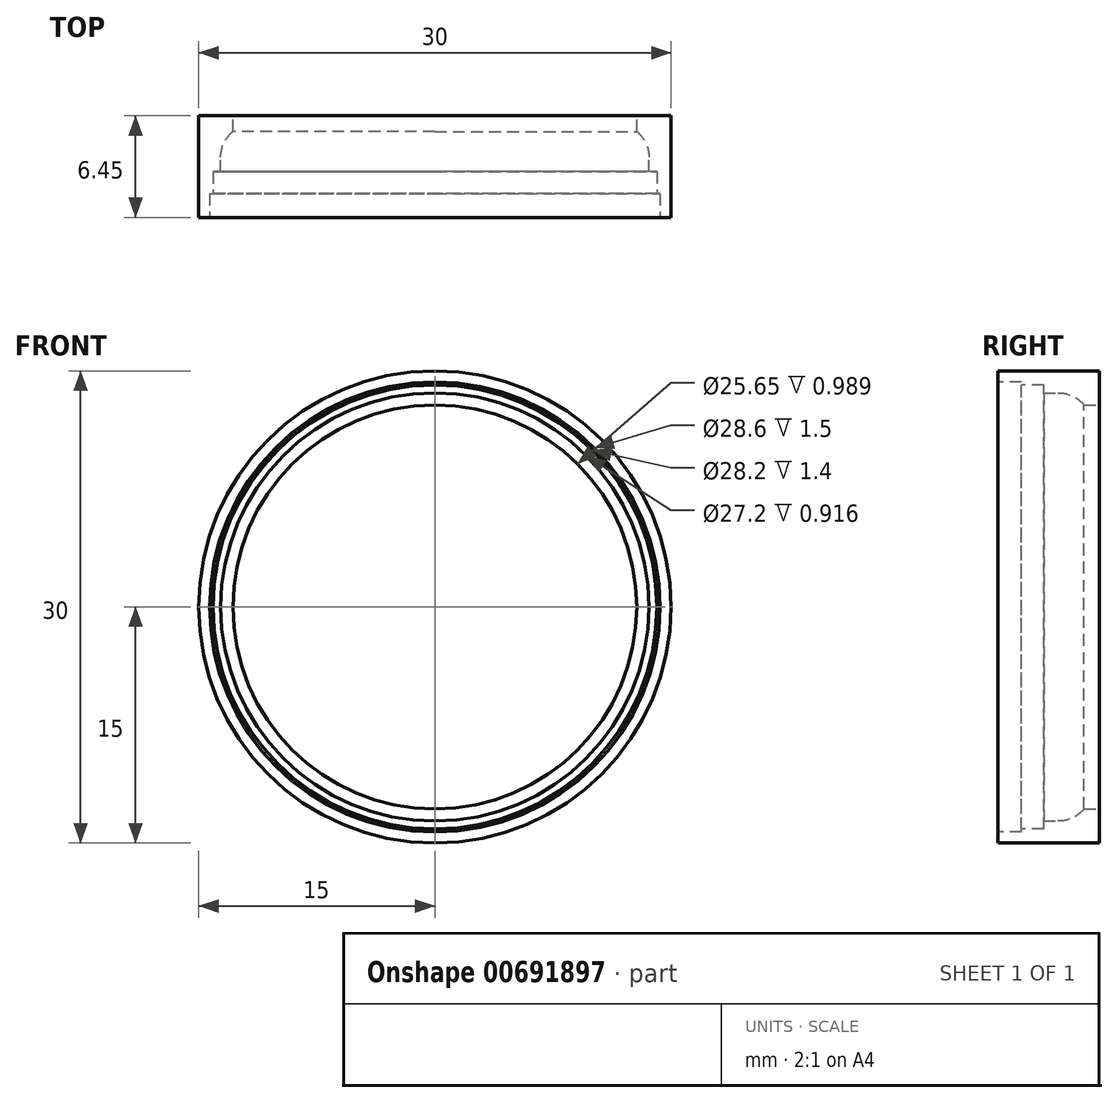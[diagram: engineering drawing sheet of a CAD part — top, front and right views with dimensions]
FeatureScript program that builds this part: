
annotation { "Feature Type Name" : "Feature", "Feature Type Description" : "" }
export const myFeature = defineFeature(function(context is Context, id is Id, definition is map)
    precondition{}
    {
        {
            var Q0;
            Q0=qCreatedBy(makeId("Front.planeOp"),FACE);
            var sketch = newSketch(context, id + "F0", { "sketchPlane" : qUnion([Q0])});
            skCircle(sketch, "E0", {"center": v(0, 0) * mm, "radius": 15 * mm});
            skCircle(sketch, "E1", {"center": v(0, 0) * mm, "radius": 12.82 * mm});
            skSolve(sketch);
        }
        {
            var Q0;
            Q0 = qSketchRegion(id + "F0", true);
            extrude(context, id + "F1", {"entities" : qUnion([Q0]), "depth" : 6.45 * mm, "offsetDistance" : 25.4 * mm});
        }
        {
            var Q0;
            Q0=makeQuery(id+"F1.opExtrude","CAP_FACE",FACE,{"disambiguationData":[OSD([sQuery(id+"F0.wireOp",EDGE,"E0"),sQuery(id+"F0.wireOp",EDGE,"E1")])],"isStart":false});
            var sketch = newSketch(context, id + "F2", { "sketchPlane" : qUnion([Q0])});
            skCircle(sketch, "E2", {"center": v(0, 0) * mm, "radius": 14.3 * mm});
            skSolve(sketch);
        }
        {
            var Q0;
            Q0 = qSketchRegion(id + "F2", true);
            extrude(context, id + "F3", {"entities" : qUnion([Q0]), "operationType" : NewBodyOperationType.REMOVE, "oppositeDirection" : true, "depth" : 1.5 * mm, "offsetDistance" : 25.4 * mm});
        }
        {
            var Q0;
            Q0=makeQuery(id+"F3.boolean.opBoolean","COPY",FACE,{"derivedFrom":makeQuery(id+"F3.opExtrude","CAP_FACE",FACE,{"disambiguationData":[OSD([sQuery(id+"F2.wireOp",EDGE,"E2")])],"isStart":false})});
            var sketch = newSketch(context, id + "F4", { "sketchPlane" : qUnion([Q0])});
            skCircle(sketch, "E3", {"center": v(0, 0) * mm, "radius": 14.1 * mm});
            skSolve(sketch);
        }
        {
            var Q0;
            Q0 = qSketchRegion(id + "F4", true);
            extrude(context, id + "F5", {"entities" : qUnion([Q0]), "operationType" : NewBodyOperationType.REMOVE, "oppositeDirection" : true, "depth" : 2.9 * mm - 1.5 * mm, "offsetDistance" : 25.4 * mm});
        }
        {
            var Q0;
            Q0=qCreatedBy(makeId("Right.planeOp"),FACE);
            var sketch = newSketch(context, id + "F6", { "sketchPlane" : qUnion([Q0])});
            skLineSegment(sketch, "E4", {"start": v(0, -15) * mm, "end": v(0, -8.73) * mm, "construction": true});
            skLineSegment(sketch, "E5.0", {"start": v(-0.5, -11.47) * mm, "end": v(-0.5, 0) * mm});
            skLineSegment(sketch, "E6", {"start": v(-3.55, -14.1) * mm, "end": v(1.09, -14.1) * mm, "construction": true});
            skPoint(sketch, "E7", {"position": v(-3.55, -14.86) * mm});
            skArc(sketch, "E8", {"start": v(-2.63, -13.6) * mm, "mid": v(-1.13, -12.97) * mm, "end": v(-0.5, -11.47) * mm});
            skLineSegment(sketch, "E9", {"start": v(-6.45, 15) * mm, "end": v(0, 15) * mm});
            skLineSegment(sketch, "E10.0", {"start": v(-3.55, -13.6) * mm, "end": v(-3.55, 0) * mm});
            skLineSegment(sketch, "E11.0", {"start": v(-3.55, -13.6) * mm, "end": v(-2.63, -13.6) * mm});
            skLineSegment(sketch, "E12", {"start": v(-3.55, 0) * mm, "end": v(-0.5, 0) * mm});
            skPoint(sketch, "E13.orphan", {"position": v(-3.55, 14.1) * mm});
            skSolve(sketch);
        }
        {
            var Q0;
            Q0 = qSketchRegion(id + "F6", true);
            var Q1;
            Q1=sQuery(id+"F6.wireOp",EDGE,"E12");
            revolve(context, id + "F7", {"operationType" : NewBodyOperationType.REMOVE, "entities" : qUnion([Q0]), "axis" : qUnion([Q1]), "revolveType" : RevolveType.FULL, "oppositeDirection" : true});
        }
    });
